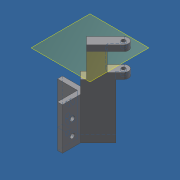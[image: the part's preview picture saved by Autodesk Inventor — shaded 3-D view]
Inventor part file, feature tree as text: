
AUTODESK INVENTOR PART (.ipt)
format: ipt  version: 2021 (Build 250183000, 183)  size: 172,544 bytes
history: native  units: mm
features: extrude x7, sketch x7, other x1, plane x1, projected_geometry x1
ambient origin geometry x8: Origin, YZ Plane, XZ Plane, XY Plane, X Axis, Y Axis, Z Axis, Center Point
bodies: Solid1 (feature_tree)
feature tree (17):
  other  "<userpath>\OneDrive\Objet3D\3DPrinter\Parameters.xlsx"
  extrude  "Extrusion1"  Depth=20.0mm
  plane  "Work Plane1"
  sketch  "Sketch3"  dims[d2=5.0mm d3=5.0mm]
  extrude  "Extrusion3"  Depth=5.0mm
  extrude  "Extrusion5"  Depth=30.0mm
  sketch  "Sketch8"  dims[d8=23.0mm d9=3.7mm]
  extrude  "Extrusion8"  Depth=3.7mm
  extrude  "Extrusion9"  Depth=25.0mm
  extrude  "Extrusion10"  Depth=5.0mm
  extrude  "Extrusion11"  Depth=55.0mm TaperAngle=0.0deg
  sketch  "Sketch1"  dims[d0=20.0mm d1=20.0mm]
  sketch  "Sketch5"  dims[d5=30.0mm d6=0.0mm d7=23.0mm]
  projected_geometry  "Projected Loop2"
  sketch  "Sketch9"  dims[d10=-6.0mm d13=25.0mm]
  sketch  "Sketch10"  dims[d16=18.0mm d17=0.0mm d18=5.0mm]
  sketch  "Sketch11"  dims[d19=135.0deg d22=55.0mm d23=0.0mm d40=4.5mm d41=10.0mm d42=10.0mm d43=4.5mm d44=10.0mm d45=15.0mm d46=10.0mm d47=10.0mm d48=10.0mm d49=15.0mm d50=4.5mm d51=4.5mm d52=20.0mm d53=0.0mm d54=20.0mm d55=0.0mm d56=135.0deg d57=0.0mm d58=43.0mm d59=0.0mm d60=25.0mm d61=55.0mm d62=0.0mm]
